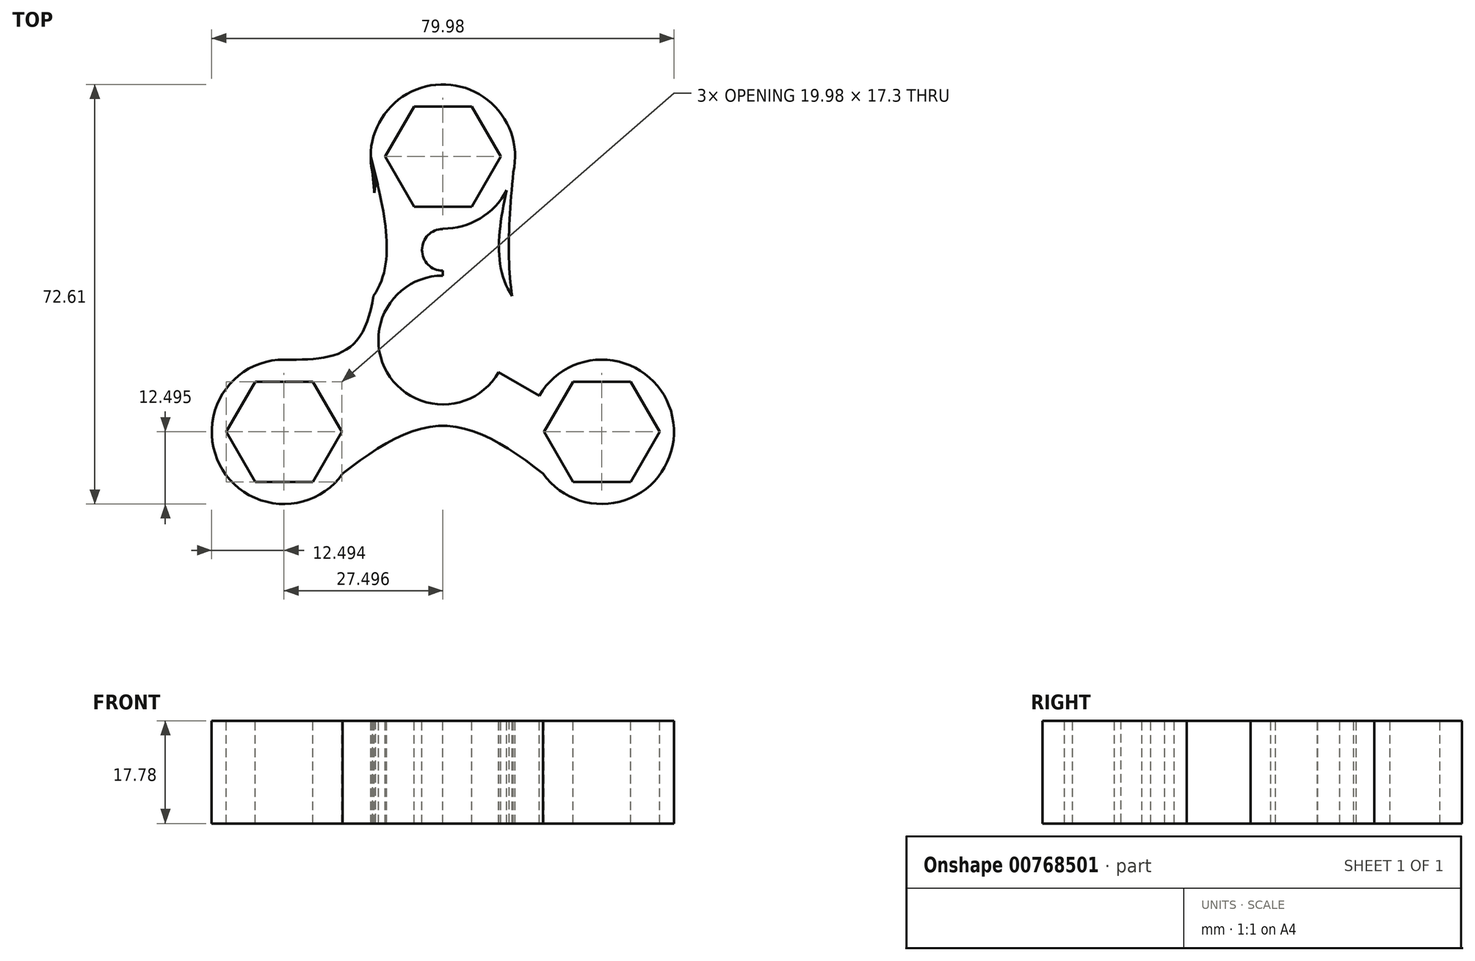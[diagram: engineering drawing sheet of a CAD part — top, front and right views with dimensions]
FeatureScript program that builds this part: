
annotation { "Feature Type Name" : "Feature", "Feature Type Description" : "" }
export const myFeature = defineFeature(function(context is Context, id is Id, definition is map)
    precondition{}
    {
        {
            var Q0;
            Q0=qCreatedBy(makeId("Top.planeOp"),FACE);
            var sketch = newSketch(context, id + "F0", { "sketchPlane" : qUnion([Q0])});
            skCircle(sketch, "E0", {"center": v(0, 0) * mm, "radius": 11.15 * mm});
            skLineSegment(sketch, "E1", {"start": v(0, 0) * mm, "end": v(0, 31.75) * mm});
            skCircle(sketch, "E2.cCircle", {"center": v(0, 31.75) * mm, "radius": 8.65 * mm, "construction": true});
            skLineSegment(sketch, "E2.0", {"start": v(-5, 40.4) * mm, "end": v(5, 40.4) * mm});
            skLineSegment(sketch, "E2.1", {"start": v(5, 40.4) * mm, "end": v(9.99, 31.75) * mm});
            skLineSegment(sketch, "E2.2", {"start": v(9.99, 31.75) * mm, "end": v(5, 23.1) * mm});
            skLineSegment(sketch, "E2.3", {"start": v(5, 23.1) * mm, "end": v(-5, 23.1) * mm});
            skLineSegment(sketch, "E2.4", {"start": v(-5, 23.1) * mm, "end": v(-9.99, 31.75) * mm});
            skLineSegment(sketch, "E2.5", {"start": v(-9.99, 31.75) * mm, "end": v(-5, 40.4) * mm});
            skPoint(sketch, "E2.0.midPoint", {"position": v(0, 40.4) * mm});
            skCircle(sketch, "E3.1.0", {"center": v(-27.5, -15.87) * mm, "radius": 8.65 * mm, "construction": true});
            skCircle(sketch, "E3.2.0", {"center": v(27.5, -15.87) * mm, "radius": 8.65 * mm, "construction": true});
            skLineSegment(sketch, "E4.0", {"start": v(-32.5, -7.22) * mm, "end": v(-22.5, -7.22) * mm});
            skLineSegment(sketch, "E4.1", {"start": v(-22.5, -7.22) * mm, "end": v(-17.5, -15.88) * mm});
            skLineSegment(sketch, "E4.2", {"start": v(-17.5, -15.88) * mm, "end": v(-22.5, -24.53) * mm});
            skLineSegment(sketch, "E4.3", {"start": v(-22.5, -24.53) * mm, "end": v(-32.5, -24.53) * mm});
            skLineSegment(sketch, "E4.4", {"start": v(-32.5, -24.52) * mm, "end": v(-37.48, -15.87) * mm});
            skLineSegment(sketch, "E4.5", {"start": v(-37.48, -15.87) * mm, "end": v(-32.5, -7.22) * mm});
            skPoint(sketch, "E4.0.midPoint", {"position": v(-27.5, -7.22) * mm});
            skLineSegment(sketch, "E5.0", {"start": v(22.5, -7.22) * mm, "end": v(32.5, -7.22) * mm});
            skLineSegment(sketch, "E5.1", {"start": v(32.5, -7.22) * mm, "end": v(37.48, -15.87) * mm});
            skLineSegment(sketch, "E5.2", {"start": v(37.48, -15.87) * mm, "end": v(32.5, -24.52) * mm});
            skLineSegment(sketch, "E5.3", {"start": v(32.5, -24.52) * mm, "end": v(22.5, -24.52) * mm});
            skLineSegment(sketch, "E5.4", {"start": v(22.5, -24.52) * mm, "end": v(17.5, -15.87) * mm});
            skLineSegment(sketch, "E5.5", {"start": v(17.5, -15.87) * mm, "end": v(22.5, -7.22) * mm});
            skPoint(sketch, "E5.0.midPoint", {"position": v(27.5, -7.22) * mm});
            skLineSegment(sketch, "E6", {"start": v(-27.5, -15.87) * mm, "end": v(0, 0) * mm});
            skLineSegment(sketch, "E7", {"start": v(0, 0) * mm, "end": v(27.5, -15.88) * mm});
            skCircle(sketch, "E8", {"center": v(-27.5, -15.87) * mm, "radius": 12.5 * mm});
            skCircle(sketch, "E9", {"center": v(27.5, -15.87) * mm, "radius": 12.5 * mm});
            skCircle(sketch, "E10", {"center": v(0, 31.75) * mm, "radius": 12.5 * mm});
            skLineSegment(sketch, "E11", {"start": v(-12.5, 31.75) * mm, "end": v(12.5, 31.75) * mm, "construction": true});
            skPoint(sketch, "E12.end.orphan", {"position": v(27.5, -3.38) * mm});
            skFitSpline(sketch, "E13", {"points": [v(27.5, -3.38) * mm, v(14.83, 0) * mm, v(12.5, 31.75) * mm], "startDerivative": vector(-41.2, -0.13) * mm, "endDerivative": vector(7.7, 66.35) * mm});
            skPoint(sketch, "E14", {"position": v(-27.5, -3.38) * mm});
            skLineSegment(sketch, "E15", {"start": v(-27.5, -3.38) * mm, "end": v(-27.5, -3.38) * mm});
            skFitSpline(sketch, "E16.trimOffspring", {"points": [v(-27.5, -3.38) * mm, v(-14.83, 0) * mm, v(-12.5, 31.75) * mm], "startDerivative": vector(41.2, -0.13) * mm, "endDerivative": vector(-7.7, 66.35) * mm});
            skPoint(sketch, "E17.0.internal.orphan", {"position": v(-22.5, -27.32) * mm});
            skFitSpline(sketch, "E18", {"points": [v(-27.5, -3.38) * mm, v(-12.2, 29.04) * mm, v(-27.5, 29.04) * mm], "startDerivative": vector(44.86, 70.2) * mm, "endDerivative": vector(-51.6, -10.65) * mm});
            skPoint(sketch, "E19.start.orphan", {"position": v(-11.15, 0) * mm});
            skPoint(sketch, "E20.start.orphan", {"position": v(11.15, 0) * mm});
            skFitSpline(sketch, "E21", {"points": [v(-27.5, -3.38) * mm, v(-10.92, 9.54) * mm, v(-12.5, 31.75) * mm], "startDerivative": vector(42.96, 22.17) * mm, "endDerivative": vector(-12.43, 48.3) * mm});
            skFitSpline(sketch, "E22", {"points": [v(27.5, -3.38) * mm, v(10.92, 9.54) * mm, v(12.5, 31.75) * mm], "startDerivative": vector(-42.96, 22.17) * mm, "endDerivative": vector(12.43, 48.3) * mm});
            skFitSpline(sketch, "E23", {"points": [v(-22.5, -27.32) * mm, v(0, -14.83) * mm, v(22.5, -27.32) * mm], "startDerivative": vector(45.14, 37.08) * mm, "endDerivative": vector(45.14, -37.08) * mm});
            skPoint(sketch, "E24.start.orphan", {"position": v(0, -11.15) * mm});
            skSolve(sketch);
        }
        {
            var Q0;
            {var subQ1=sQuery(id+"F0.wireOp",EDGE,"E6");var subQ3=sQuery(id+"F0.wireOp",EDGE,"E0");var subQ4=makeQuery(id+"F0.imprint","INTERSECT",VERTEX,{"derivedFrom":[subQ3,subQ1]});Q0=makeQuery(id+"F0.imprint","IMPRINT",FACE,{"disambiguationData":[TD([[makeQuery(id+"F0.imprint","IMPRINT",EDGE,{"disambiguationData":[TD([[subQ4,1.0]])],"derivedFrom":subQ3}),-1.0]])]});}
            var Q1;
            {var subQ6=sQuery(id+"F0.wireOp",EDGE,"E4.0");Q1=makeQuery(id+"F0.imprint","IMPRINT",FACE,{"disambiguationData":[TD([[makeQuery(id+"F0.imprint","IMPRINT",EDGE,{"derivedFrom":subQ6}),1.0]])]});}
            var Q2;
            {var subQ1=sQuery(id+"F0.wireOp",EDGE,"E6");var subQ9=sQuery(id+"F0.wireOp",EDGE,"E0");var subQ11=makeQuery(id+"F0.imprint","INTERSECT",VERTEX,{"derivedFrom":[subQ9,subQ1]});Q2=makeQuery(id+"F0.imprint","IMPRINT",FACE,{"disambiguationData":[TD([[makeQuery(id+"F0.imprint","IMPRINT",EDGE,{"disambiguationData":[TD([[subQ11,-1.0]])],"derivedFrom":subQ9}),-1.0]])]});}
            var Q3;
            {var subQ5=sQuery(id+"F0.wireOp",EDGE,"E5.0");Q3=makeQuery(id+"F0.imprint","IMPRINT",FACE,{"disambiguationData":[TD([[makeQuery(id+"F0.imprint","IMPRINT",EDGE,{"derivedFrom":subQ5}),1.0]])]});}
            var Q4;
            {var subQ1=sQuery(id+"F0.wireOp",EDGE,"E9");var subQ3=makeQuery(id+"F0.imprint","IMPRINT",VERTEX,{"derivedFrom":subQ1});Q4=makeQuery(id+"F0.imprint","IMPRINT",FACE,{"disambiguationData":[TD([[makeQuery(id+"F0.imprint","IMPRINT",EDGE,{"disambiguationData":[TD([[subQ3,1.0]])],"derivedFrom":subQ1}),-1.0]])]});}
            var Q5;
            Q5=makeQuery(id+"F0.imprint","IMPRINT",FACE,{"disambiguationData":[TD([[makeQuery(id+"F0.imprint","IMPRINT",EDGE,{"derivedFrom":sQuery(id+"F0.wireOp",EDGE,"E2.0")}),1.0]])]});
            var Q6;
            {var subQ0=sQuery(id+"F0.wireOp",EDGE,"E23");var subQ1=sQuery(id+"F0.wireOp",EDGE,"E8");var subQ2=makeQuery(id+"F0.imprint","INTERSECT",VERTEX,{"disambiguationData":[OD(0.0)],"derivedFrom":[subQ1,subQ0]});Q6=makeQuery(id+"F0.imprint","IMPRINT",FACE,{"disambiguationData":[TD([[makeQuery(id+"F0.imprint","IMPRINT",EDGE,{"disambiguationData":[TD([[subQ2,-1.0]])],"derivedFrom":subQ1}),1.0]])]});}
            var Q7;
            {var subQ0=sQuery(id+"F0.wireOp",EDGE,"E23");var subQ1=sQuery(id+"F0.wireOp",EDGE,"E9");var subQ2=makeQuery(id+"F0.imprint","INTERSECT",VERTEX,{"disambiguationData":[OD(0.0)],"derivedFrom":[subQ1,subQ0]});Q7=makeQuery(id+"F0.imprint","IMPRINT",FACE,{"disambiguationData":[TD([[makeQuery(id+"F0.imprint","IMPRINT",EDGE,{"disambiguationData":[TD([[subQ2,1.0]])],"derivedFrom":subQ1}),1.0]])]});}
            var Q8;
            {var subQ0=sQuery(id+"F0.wireOp",EDGE,"E13");Q8=makeQuery(id+"F0.imprint","IMPRINT",FACE,{"disambiguationData":[TD([[makeQuery(id+"F0.imprint","IMPRINT",EDGE,{"derivedFrom":subQ0}),1.0]])]});}
            var Q9;
            {var subQ4=sQuery(id+"F0.wireOp",EDGE,"E16.trimOffspring");Q9=makeQuery(id+"F0.imprint","IMPRINT",FACE,{"disambiguationData":[TD([[makeQuery(id+"F0.imprint","IMPRINT",EDGE,{"derivedFrom":subQ4}),-1.0]])]});}
            var Q10;
            {var subQ0=sQuery(id+"F0.wireOp",EDGE,"E13");Q10=makeQuery(id+"F0.imprint","IMPRINT",FACE,{"disambiguationData":[TD([[makeQuery(id+"F0.imprint","IMPRINT",EDGE,{"derivedFrom":subQ0}),-1.0]])]});}
            var Q11;
            {var subQ0=sQuery(id+"F0.wireOp",EDGE,"E16.trimOffspring");Q11=makeQuery(id+"F0.imprint","IMPRINT",FACE,{"disambiguationData":[TD([[makeQuery(id+"F0.imprint","IMPRINT",EDGE,{"derivedFrom":subQ0}),1.0]])]});}
            var Q12;
            {var subQ0=sQuery(id+"F0.wireOp",EDGE,"E18");Q12=makeQuery(id+"F0.imprint","IMPRINT",FACE,{"disambiguationData":[TD([[makeQuery(id+"F0.imprint","IMPRINT",EDGE,{"derivedFrom":subQ0}),1.0]])]});}
            extrude(context, id + "F1", {"entities" : qUnion([Q0, Q1, Q2, Q3, Q4, Q5, Q6, Q7, Q8, Q9, Q10, Q11, Q12]), "oppositeDirection" : true, "depth" : 17.78 * mm, "offsetDistance" : 25.4 * mm});
        }
        {
            var Q0;
            {var subQ1=sQuery(id+"F0.wireOp",EDGE,"E6");var subQ3=sQuery(id+"F0.wireOp",EDGE,"E0");var subQ4=makeQuery(id+"F0.imprint","INTERSECT",VERTEX,{"derivedFrom":[subQ3,subQ1]});Q0=makeQuery(id+"F0.imprint","IMPRINT",FACE,{"disambiguationData":[TD([[makeQuery(id+"F0.imprint","IMPRINT",EDGE,{"disambiguationData":[TD([[subQ4,1.0]])],"derivedFrom":subQ3}),-1.0]])]});}
            var sketch = newSketch(context, id + "F2", { "sketchPlane" : qUnion([Q0])});
            skLineSegment(sketch, "E25.bottom", {"start": v(-9.91, 19.5) * mm, "end": v(9.7, 19.5) * mm});
            skLineSegment(sketch, "E25.top", {"start": v(-9.91, 11.23) * mm, "end": v(9.7, 11.23) * mm});
            skLineSegment(sketch, "E25.left", {"start": v(-9.91, 19.5) * mm, "end": v(-9.91, 11.23) * mm});
            skLineSegment(sketch, "E25.right", {"start": v(9.7, 19.5) * mm, "end": v(9.7, 11.23) * mm});
            skCircle(sketch, "E26", {"center": v(0, 15.6) * mm, "radius": 3.6 * mm});
            skSolve(sketch);
        }
        {
            var Q0;
            {var subQ0=sQuery(id+"F2.wireOp",EDGE,"E26");var subQ1=sQuery(id+"F0.wireOp",EDGE,"E1");var subQ2=makeQuery(id+"F0.imprint","IMPRINT",EDGE,{"disambiguationData":[TD([[makeQuery(id+"F0.imprint","INTERSECT",VERTEX,{"derivedFrom":[subQ1,sQuery(id+"F0.wireOp",EDGE,"E10")]}),1.0]])],"derivedFrom":subQ1});var subQ3=makeQuery(id+"F2.imprint","INTERSECT",VERTEX,{"disambiguationData":[OD(0.0)],"derivedFrom":[subQ2,subQ0]});Q0=makeQuery(id+"F2.imprint","IMPRINT",FACE,{"disambiguationData":[TD([[makeQuery(id+"F2.imprint","IMPRINT",EDGE,{"disambiguationData":[TD([[subQ3,1.0]])],"derivedFrom":subQ0}),1.0]])]});}
            var Q1;
            {var subQ0=sQuery(id+"F2.wireOp",EDGE,"E26");var subQ1=sQuery(id+"F0.wireOp",EDGE,"E1");var subQ2=makeQuery(id+"F0.imprint","IMPRINT",EDGE,{"disambiguationData":[TD([[makeQuery(id+"F0.imprint","INTERSECT",VERTEX,{"derivedFrom":[subQ1,sQuery(id+"F0.wireOp",EDGE,"E10")]}),1.0]])],"derivedFrom":subQ1});var subQ3=makeQuery(id+"F2.imprint","INTERSECT",VERTEX,{"disambiguationData":[OD(0.0)],"derivedFrom":[subQ2,subQ0]});Q1=makeQuery(id+"F2.imprint","IMPRINT",FACE,{"disambiguationData":[TD([[makeQuery(id+"F2.imprint","IMPRINT",EDGE,{"disambiguationData":[TD([[subQ3,-1.0]])],"derivedFrom":subQ0}),1.0]])]});}
            extrude(context, id + "F3", {"entities" : qUnion([Q0, Q1]), "operationType" : NewBodyOperationType.REMOVE, "oppositeDirection" : true, "depth" : 25 * mm, "offsetDistance" : 25 * mm});
        }
    });
